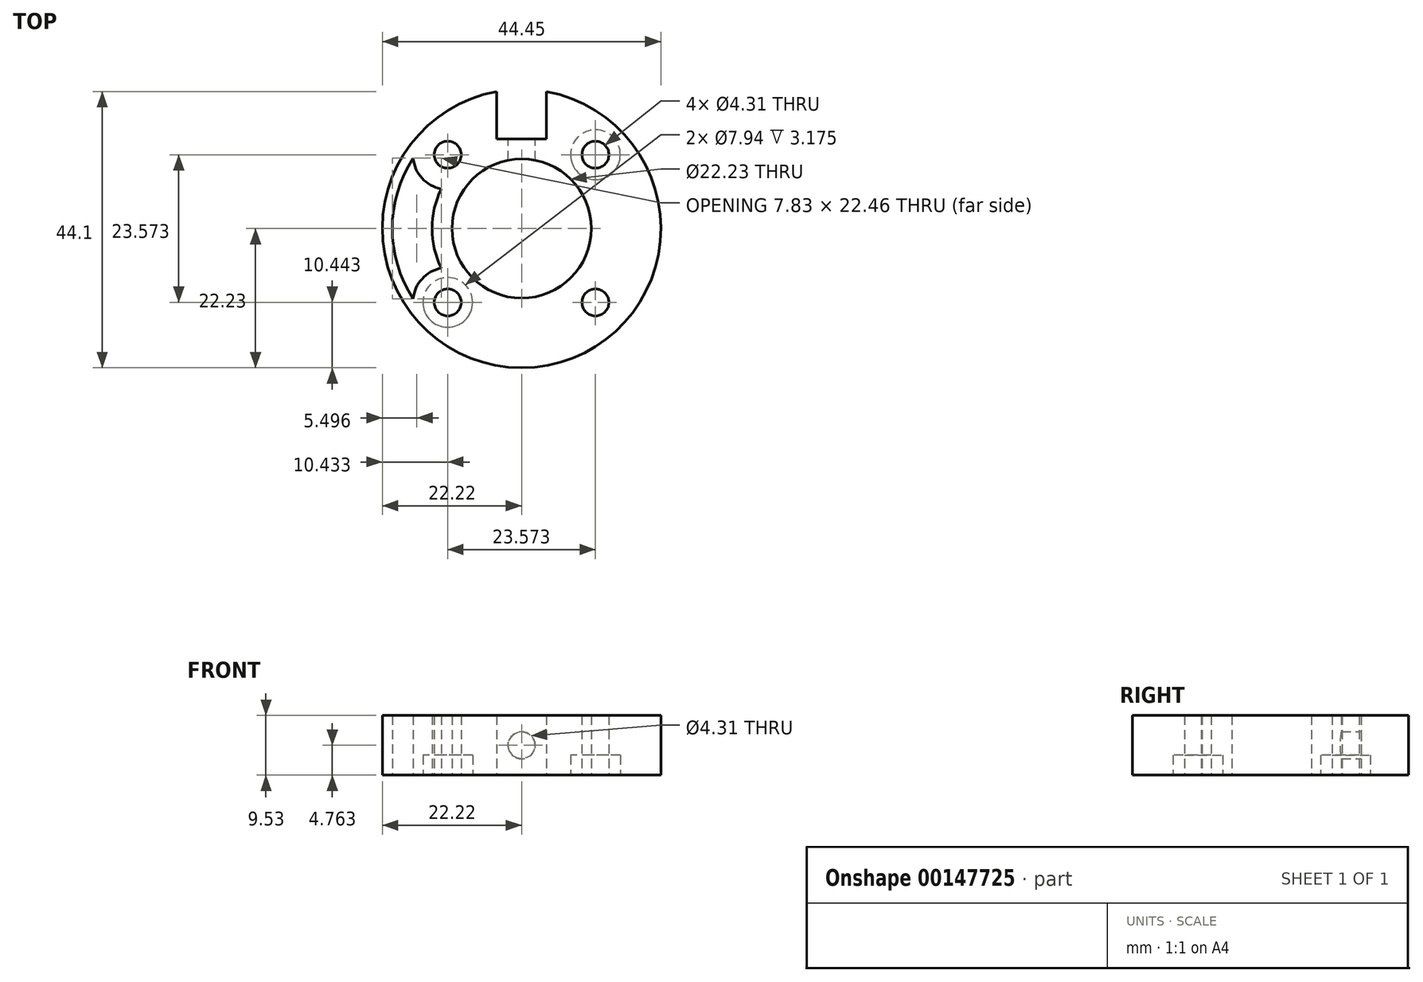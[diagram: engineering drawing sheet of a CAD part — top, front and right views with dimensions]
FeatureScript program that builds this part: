
annotation { "Feature Type Name" : "Feature", "Feature Type Description" : "" }
export const myFeature = defineFeature(function(context is Context, id is Id, definition is map)
    precondition{}
    {
        {
            var Q0;
            Q0=qCreatedBy(makeId("Top.planeOp"),FACE);
            var sketch = newSketch(context, id + "F0", { "sketchPlane" : qUnion([Q0])});
            skCircle(sketch, "E0", {"center": v(0, 0) * mm, "radius": 11.11 * mm});
            skLineSegment(sketch, "E1.bottom", {"start": v(11.79, 11.79) * mm, "end": v(-11.79, 11.79) * mm, "construction": true});
            skLineSegment(sketch, "E1.top", {"start": v(11.79, -11.79) * mm, "end": v(-11.79, -11.79) * mm, "construction": true});
            skLineSegment(sketch, "E1.left", {"start": v(11.79, 11.79) * mm, "end": v(11.79, -11.79) * mm, "construction": true});
            skLineSegment(sketch, "E1.right", {"start": v(-11.79, 11.79) * mm, "end": v(-11.79, -11.79) * mm, "construction": true});
            skCircle(sketch, "E2", {"center": v(-11.79, 11.79) * mm, "radius": 5.56 * mm, "construction": true});
            skLineSegment(sketch, "E3", {"start": v(0, 0) * mm, "end": v(0, 11.11) * mm});
            skLineSegment(sketch, "E4", {"start": v(0, 11.11) * mm, "end": v(0, 14.29) * mm});
            skLineSegment(sketch, "E5.bottom", {"start": v(-3.97, 21.87) * mm, "end": v(3.97, 21.87) * mm, "construction": true});
            skLineSegment(sketch, "E5.top", {"start": v(-3.97, 14.29) * mm, "end": v(3.97, 14.29) * mm});
            skLineSegment(sketch, "E5.left", {"start": v(-3.97, 21.87) * mm, "end": v(-3.97, 14.29) * mm});
            skLineSegment(sketch, "E5.right", {"start": v(3.97, 21.87) * mm, "end": v(3.97, 14.29) * mm});
            skArc(sketch, "E6", {"start": v(-3.97, 21.87) * mm, "mid": v(0, -22.22) * mm, "end": v(3.97, 21.87) * mm});
            skCircle(sketch, "E7", {"center": v(-11.79, 11.79) * mm, "radius": 2.15 * mm});
            skCircle(sketch, "E8", {"center": v(-11.79, -11.79) * mm, "radius": 2.15 * mm});
            skCircle(sketch, "E9", {"center": v(11.79, -11.79) * mm, "radius": 2.15 * mm});
            skCircle(sketch, "E10", {"center": v(11.79, 11.79) * mm, "radius": 2.15 * mm});
            skSolve(sketch);
        }
        {
            var Q0;
            Q0=qSketchRegion(id+"F0",true);
            extrude(context, id + "F1", {"entities" : qUnion([Q0]), "depth" : 9.52 * mm});
        }
        {
            var Q0;
            Q0=makeQuery(id+"F1.opExtrude","SWEPT_FACE",FACE,{"disambiguationData":[OSD([sQuery(id+"F0.wireOp",EDGE,"E5.top")])]});
            var sketch = newSketch(context, id + "F2", { "sketchPlane" : qUnion([Q0])});
            skLineSegment(sketch, "E11", {"start": v(0, 9.53) * mm, "end": v(0, 0) * mm, "construction": true});
            skCircle(sketch, "E12", {"center": v(0, 4.76) * mm, "radius": 2.15 * mm});
            skSolve(sketch);
        }
        {
            var Q0;
            Q0=qSketchRegion(id+"F2",true);
            var Q1;
            Q1=makeQuery(id+"F1.opExtrude","SWEPT_FACE",FACE,{"disambiguationData":[OSD([sQuery(id+"F0.wireOp",EDGE,"E0")])]});
            extrude(context, id + "F3", {"entities" : qUnion([Q0]), "operationType" : NewBodyOperationType.REMOVE, "endBound" : BoundingType.UP_TO_SURFACE, "oppositeDirection" : true, "endBoundEntityFace" : qUnion([Q1]), "depth" : 25.4 * mm});
        }
        {
            var Q0;
            Q0=makeQuery(id+"F1.opExtrude","CAP_FACE",FACE,{"disambiguationData":[OSD([sQuery(id+"F0.wireOp",EDGE,"E0"),sQuery(id+"F0.wireOp",EDGE,"E5.top"),sQuery(id+"F0.wireOp",EDGE,"E5.left"),sQuery(id+"F0.wireOp",EDGE,"E5.right"),sQuery(id+"F0.wireOp",EDGE,"E6"),sQuery(id+"F0.wireOp",EDGE,"E7"),sQuery(id+"F0.wireOp",EDGE,"E8"),sQuery(id+"F0.wireOp",EDGE,"E9"),sQuery(id+"F0.wireOp",EDGE,"E10")])],"isStart":false});
            cPlane(context, id + "F4", {"entities" : qUnion([Q0]), "cplaneType" : CPlaneType.OFFSET, "offset" : 6.35 * mm, "oppositeDirection" : true, "width" : 152.4 * mm, "height" : 152.4 * mm});
        }
        {
            var Q0;
            Q0=makeQuery(id+"F1.opExtrude","CAP_FACE",FACE,{"disambiguationData":[OSD([sQuery(id+"F0.wireOp",EDGE,"E0"),sQuery(id+"F0.wireOp",EDGE,"E5.top"),sQuery(id+"F0.wireOp",EDGE,"E5.left"),sQuery(id+"F0.wireOp",EDGE,"E5.right"),sQuery(id+"F0.wireOp",EDGE,"E6"),sQuery(id+"F0.wireOp",EDGE,"E7"),sQuery(id+"F0.wireOp",EDGE,"E8"),sQuery(id+"F0.wireOp",EDGE,"E9"),sQuery(id+"F0.wireOp",EDGE,"E10")])],"isStart":true});
            var sketch = newSketch(context, id + "F5", { "sketchPlane" : qUnion([Q0])});
            skCircle(sketch, "E13", {"center": v(11.79, -11.79) * mm, "radius": 3.97 * mm});
            skCircle(sketch, "E14", {"center": v(-11.79, 11.79) * mm, "radius": 3.97 * mm});
            skSolve(sketch);
        }
        {
            var Q0;
            Q0=qSketchRegion(id+"F5",true);
            var Q1;
            Q1=qCreatedBy(id+"F4.planeOp",FACE);
            extrude(context, id + "F6", {"entities" : qUnion([Q0]), "operationType" : NewBodyOperationType.REMOVE, "endBound" : BoundingType.UP_TO_SURFACE, "oppositeDirection" : true, "endBoundEntityFace" : qUnion([Q1]), "depth" : 25.4 * mm});
        }
        {
            var Q0;
            Q0=makeQuery(id+"F1.opExtrude","CAP_FACE",FACE,{"disambiguationData":[OSD([sQuery(id+"F0.wireOp",EDGE,"E0"),sQuery(id+"F0.wireOp",EDGE,"E5.top"),sQuery(id+"F0.wireOp",EDGE,"E5.left"),sQuery(id+"F0.wireOp",EDGE,"E5.right"),sQuery(id+"F0.wireOp",EDGE,"E6"),sQuery(id+"F0.wireOp",EDGE,"E7"),sQuery(id+"F0.wireOp",EDGE,"E8"),sQuery(id+"F0.wireOp",EDGE,"E9"),sQuery(id+"F0.wireOp",EDGE,"E10")])],"isStart":true});
            var sketch = newSketch(context, id + "F7", { "sketchPlane" : qUnion([Q0])});
            skArc(sketch, "E15", {"start": v(-12.81, -6.33) * mm, "mid": v(-15.88, -8.03) * mm, "end": v(-17.31, -11.23) * mm});
            skArc(sketch, "E16", {"start": v(-17.31, 11.23) * mm, "mid": v(-15.88, 8.03) * mm, "end": v(-12.81, 6.33) * mm});
            skArc(sketch, "E17", {"start": v(-17.31, 11.23) * mm, "mid": v(-20.64, 0) * mm, "end": v(-17.31, -11.23) * mm});
            skArc(sketch, "E18", {"start": v(-12.81, 6.33) * mm, "mid": v(-14.29, 0) * mm, "end": v(-12.81, -6.33) * mm});
            skSolve(sketch);
        }
        {
            var Q0;
            Q0=qSketchRegion(id+"F7",true);
            var Q1;
            Q1=makeQuery(id+"F1.opExtrude","CAP_FACE",FACE,{"disambiguationData":[OSD([sQuery(id+"F0.wireOp",EDGE,"E0"),sQuery(id+"F0.wireOp",EDGE,"E5.top"),sQuery(id+"F0.wireOp",EDGE,"E5.left"),sQuery(id+"F0.wireOp",EDGE,"E5.right"),sQuery(id+"F0.wireOp",EDGE,"E6"),sQuery(id+"F0.wireOp",EDGE,"E7"),sQuery(id+"F0.wireOp",EDGE,"E8"),sQuery(id+"F0.wireOp",EDGE,"E9"),sQuery(id+"F0.wireOp",EDGE,"E10")])],"isStart":false});
            extrude(context, id + "F8", {"entities" : qUnion([Q0]), "operationType" : NewBodyOperationType.REMOVE, "endBound" : BoundingType.UP_TO_SURFACE, "oppositeDirection" : true, "endBoundEntityFace" : qUnion([Q1]), "depth" : 25.4 * mm});
        }
    });
